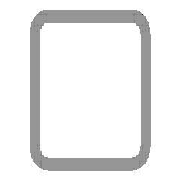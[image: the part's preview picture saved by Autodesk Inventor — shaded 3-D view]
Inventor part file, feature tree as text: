
AUTODESK INVENTOR PART (.ipt)
format: ipt  version: 2022 (Build 260153000, 153)  size: 136,192 bytes
history: native  units: mm (DEFAULTED — no unit token found)
features: other x4, sketch x3, plane x1
ambient origin geometry x8: Origin, YZ Plane, XZ Plane, XY Plane, X Axis, Y Axis, Z Axis, Center Point
bodies: Solid1 (feature_tree), Body (feature_tree)
feature tree (8):
  parser-record x1  (decoder bookkeeping rows leaked as tree rows — omitted from the tree; the rows remain in map.json)
  other  "Driven Length"
  other  "Start Plane"
  other  "End Plane"
  sketch  "Sketch"  dims[d7=7.5mm d10=40.0mm d11=40.0mm d12=5.0mm d13=-0.0mm d14=450.0mm d15=20.0mm d16=20.0mm d17=90.0deg d18=450.0mm]
  sketch  "Sketch3"  dims[d3=450.0mm]
  plane  "Work Plane3"
  sketch  "Sketch4"  dims[d4=0.0mm]
